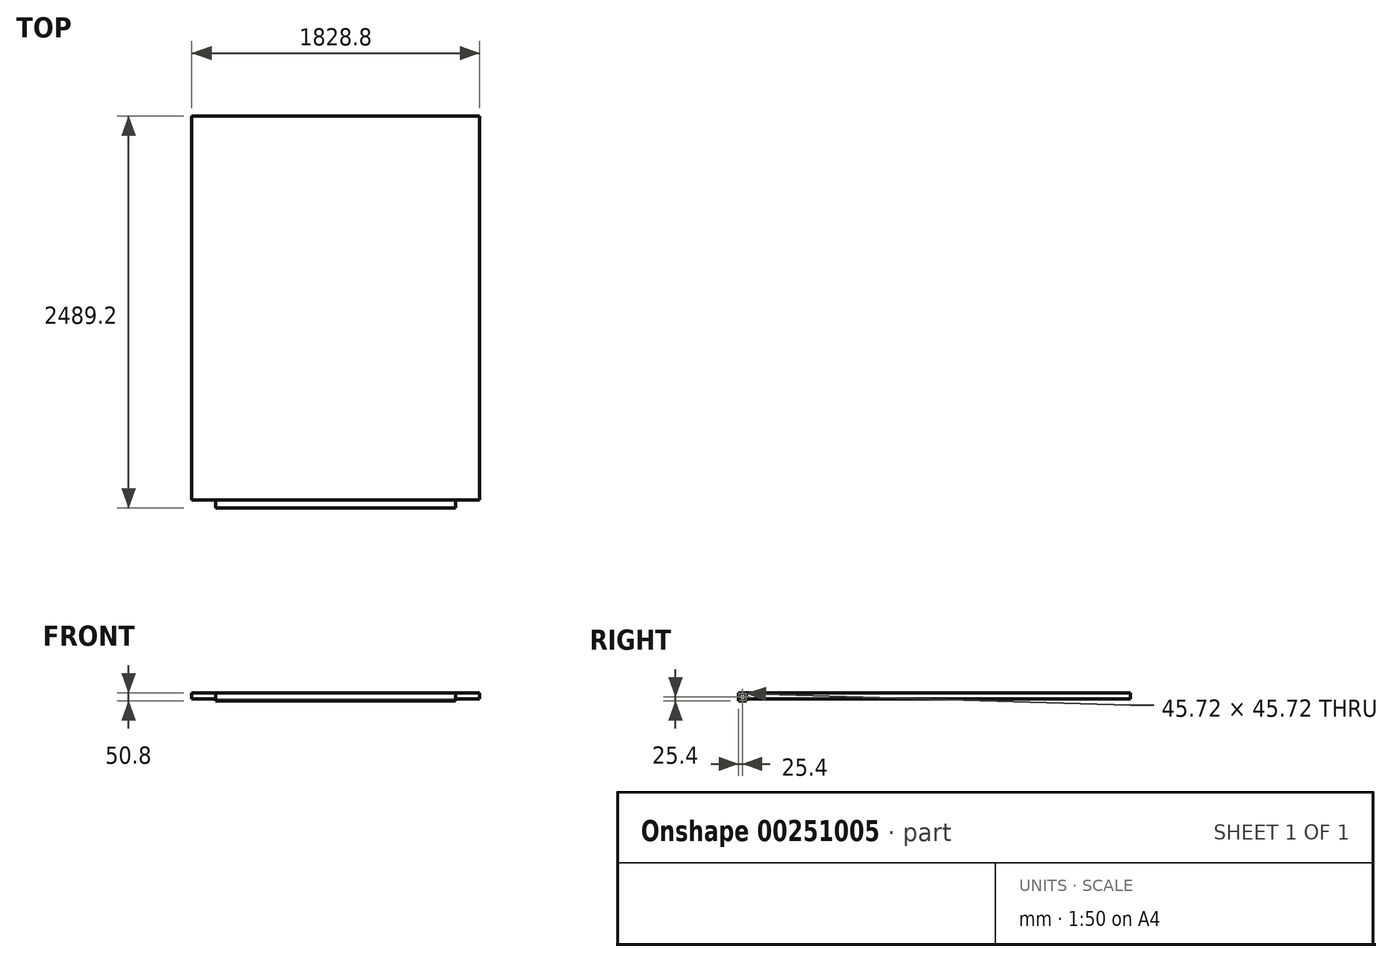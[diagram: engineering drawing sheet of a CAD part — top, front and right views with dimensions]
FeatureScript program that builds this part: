
annotation { "Feature Type Name" : "Feature", "Feature Type Description" : "" }
export const myFeature = defineFeature(function(context is Context, id is Id, definition is map)
    precondition{}
    {
        {
            var Q0;
            Q0=qCreatedBy(makeId("Top.planeOp"),FACE);
            var sketch = newSketch(context, id + "F0", { "sketchPlane" : qUnion([Q0])});
            skLineSegment(sketch, "E0.bottom", {"start": v(-914.4, 1219.2) * mm, "end": v(914.4, 1219.2) * mm});
            skLineSegment(sketch, "E0.top", {"start": v(-914.4, -1219.2) * mm, "end": v(914.4, -1219.2) * mm});
            skLineSegment(sketch, "E0.left", {"start": v(-914.4, 1219.2) * mm, "end": v(-914.4, -1219.2) * mm});
            skLineSegment(sketch, "E0.right", {"start": v(914.4, 1219.2) * mm, "end": v(914.4, -1219.2) * mm});
            skPoint(sketch, "E0.middle", {"position": v(0, 0) * mm});
            skSolve(sketch);
        }
        {
            var Q0;
            Q0=makeQuery(id+"F0.imprint","IMPRINT",FACE,{"disambiguationData":[TD([[makeQuery(id+"F0.imprint","IMPRINT",EDGE,{"derivedFrom":sQuery(id+"F0.wireOp",EDGE,"E0.bottom")}),-1.0]])]});
            extrude(context, id + "F1", {"entities" : qUnion([Q0]), "depth" : 38.1 * mm});
        }
        {
            var Q0;
            Q0=makeQuery(id+"F1.opExtrude","CAP_FACE",FACE,{"disambiguationData":[OSD([sQuery(id+"F0.wireOp",EDGE,"E0.bottom"),sQuery(id+"F0.wireOp",EDGE,"E0.top"),sQuery(id+"F0.wireOp",EDGE,"E0.left"),sQuery(id+"F0.wireOp",EDGE,"E0.right")])],"isStart":false});
            var sketch = newSketch(context, id + "F2", { "sketchPlane" : qUnion([Q0])});
            skLineSegment(sketch, "E1.bottom", {"start": v(-762, -1219.2) * mm, "end": v(762, -1219.2) * mm});
            skLineSegment(sketch, "E1.top", {"start": v(-762, -1270) * mm, "end": v(762, -1270) * mm});
            skLineSegment(sketch, "E1.left", {"start": v(-762, -1219.2) * mm, "end": v(-762, -1270) * mm});
            skLineSegment(sketch, "E1.right", {"start": v(762, -1219.2) * mm, "end": v(762, -1270) * mm});
            skSolve(sketch);
        }
        {
            var Q0;
            Q0 = qSketchRegion(id + "F2", true);
            extrude(context, id + "F3", {"entities" : qUnion([Q0]), "oppositeDirection" : true, "depth" : 50.8 * mm});
        }
        {
            var Q0;
            Q0=makeQuery(id+"F3.opExtrude","SWEPT_FACE",FACE,{"disambiguationData":[OSD([sQuery(id+"F2.wireOp",EDGE,"E1.right")])]});
            var Q1;
            Q1=makeQuery(id+"F3.opExtrude","SWEPT_FACE",FACE,{"disambiguationData":[OSD([sQuery(id+"F2.wireOp",EDGE,"E1.left")])]});
            shell(context, id + "F4", {"entities" : qUnion([Q0, Q1]), "thickness" : 2.54 * mm});
        }
    });
